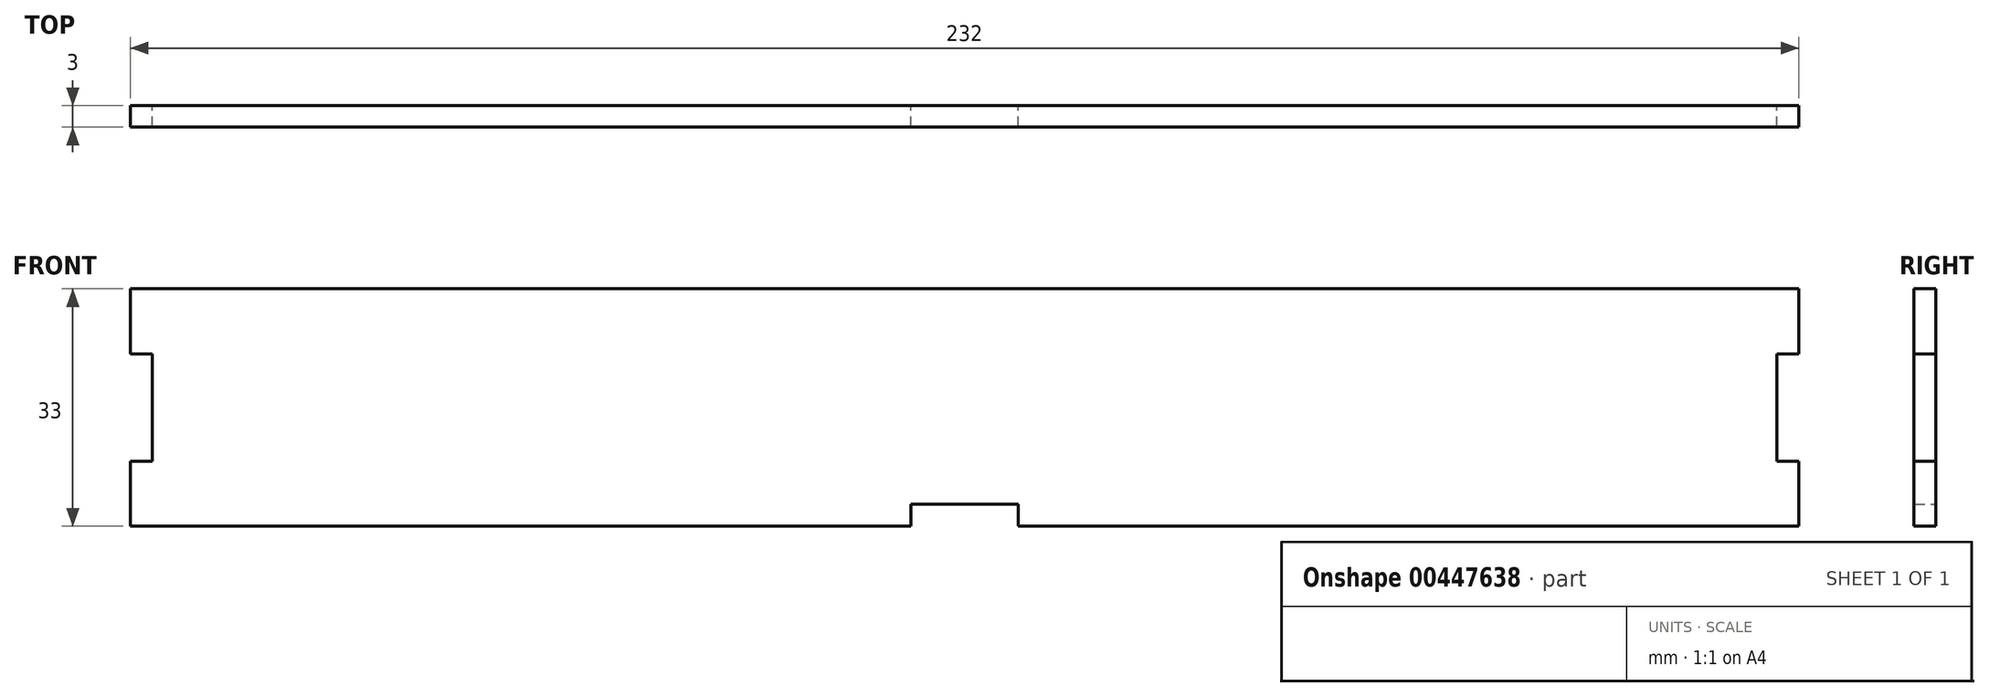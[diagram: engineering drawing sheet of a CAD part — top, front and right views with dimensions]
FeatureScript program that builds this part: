
annotation { "Feature Type Name" : "Feature", "Feature Type Description" : "" }
export const myFeature = defineFeature(function(context is Context, id is Id, definition is map)
    precondition{}
    {
        {
            var Q0;
            Q0=qCreatedBy(makeId("Front.planeOp"),FACE);
            var sketch = newSketch(context, id + "F0", { "sketchPlane" : qUnion([Q0])});
            skLineSegment(sketch, "E0.bottom", {"start": v(116, -16.5) * mm, "end": v(-116, -16.5) * mm});
            skLineSegment(sketch, "E0.top", {"start": v(116, 16.5) * mm, "end": v(-116, 16.5) * mm});
            skLineSegment(sketch, "E0.left", {"start": v(116, -16.5) * mm, "end": v(116, 16.5) * mm});
            skLineSegment(sketch, "E0.right", {"start": v(-116, -16.5) * mm, "end": v(-116, 16.5) * mm});
            skPoint(sketch, "E0.middle", {"position": v(0, 0) * mm});
            skLineSegment(sketch, "E1.bottom", {"start": v(7.45, -16.5) * mm, "end": v(-7.45, -16.5) * mm});
            skLineSegment(sketch, "E1.top", {"start": v(7.45, -13.45) * mm, "end": v(-7.45, -13.45) * mm});
            skLineSegment(sketch, "E1.left", {"start": v(7.45, -16.5) * mm, "end": v(7.45, -13.45) * mm});
            skLineSegment(sketch, "E1.right", {"start": v(-7.45, -16.5) * mm, "end": v(-7.45, -13.45) * mm});
            skPoint(sketch, "E1.middle", {"position": v(0, -14.98) * mm});
            skLineSegment(sketch, "E2.bottom", {"start": v(-112.95, -7.45) * mm, "end": v(-116, -7.45) * mm});
            skLineSegment(sketch, "E2.top", {"start": v(-112.95, 7.45) * mm, "end": v(-116, 7.45) * mm});
            skLineSegment(sketch, "E2.left", {"start": v(-112.95, -7.45) * mm, "end": v(-112.95, 7.45) * mm});
            skLineSegment(sketch, "E2.right", {"start": v(-116, -7.45) * mm, "end": v(-116, 7.45) * mm});
            skPoint(sketch, "E2.middle", {"position": v(-114.48, 0) * mm});
            skLineSegment(sketch, "E3.bottom", {"start": v(116, -7.45) * mm, "end": v(112.95, -7.45) * mm});
            skLineSegment(sketch, "E3.top", {"start": v(116, 7.45) * mm, "end": v(112.95, 7.45) * mm});
            skLineSegment(sketch, "E3.left", {"start": v(116, -7.45) * mm, "end": v(116, 7.45) * mm});
            skLineSegment(sketch, "E3.right", {"start": v(112.95, -7.45) * mm, "end": v(112.95, 7.45) * mm});
            skPoint(sketch, "E3.middle", {"position": v(114.48, 0) * mm});
            skLineSegment(sketch, "E4.bottom", {"start": v(7.5, 16.5) * mm, "end": v(-7.5, 16.5) * mm});
            skLineSegment(sketch, "E4.top", {"start": v(7.5, 19.55) * mm, "end": v(-7.5, 19.55) * mm});
            skLineSegment(sketch, "E4.left", {"start": v(7.5, 16.5) * mm, "end": v(7.5, 19.55) * mm});
            skLineSegment(sketch, "E4.right", {"start": v(-7.5, 16.5) * mm, "end": v(-7.5, 19.55) * mm});
            skPoint(sketch, "E4.middle", {"position": v(0, 18.02) * mm});
            skSolve(sketch);
        }
        {
            var Q0;
            Q0=makeQuery(id+"F0.imprint","IMPRINT",FACE,{"disambiguationData":[TD([[makeQuery(id+"F0.imprint","IMPRINT",EDGE,{"derivedFrom":sQuery(id+"F0.wireOp",EDGE,"E4.bottom")}),-1.0]])]});
            var Q1;
            Q1=makeQuery(id+"F0.imprint","IMPRINT",FACE,{"disambiguationData":[TD([[makeQuery(id+"F0.imprint","IMPRINT",EDGE,{"derivedFrom":sQuery(id+"F0.wireOp",EDGE,"E1.top")}),-1.0]])]});
            extrude(context, id + "F1", {"entities" : qUnion([Q0, Q1]), "depth" : 3 * mm});
        }
    });
